# Revit family: Casement_41_E_Side_Hung_SD_Custom
name_source: partatom
category: Windows
revit_build: Autodesk Revit 2014 (Build: 20130308_1515(x64)
units: mm (PartAtom-declared; Revit-internal decimal feet)

## types (1)
- 41-TypeE-S-SD-Custom
    Corrected Mullion Configuration = 2 mm  [stored 0.00656168 ft]
    Description = Window 41mm, Type E, Side hung, Standard sash, Custom
    Frame Profile Thickness = 41 mm  [stored 0.134514 ft]
    Heavy Duty Sash = No
    Limit Fixed Pane Height Max = 3000 mm  [stored 9.84252 ft]
    Limit Fixed Pane Height Min = 200 mm  [stored 0.656168 ft]
    Limit Fixed Pane Width Max = 3000 mm  [stored 9.84252 ft]
    Limit Fixed Pane Width Min = 200 mm  [stored 0.656168 ft]
    Limit Sash Height Max = 1500 mm  [stored 4.92126 ft]
    Limit Sash Height Min = 300 mm  [stored 0.984252 ft]
    Limit Sash Width Max = 700 mm  [stored 2.29659 ft]
    Limit Sash Width Min = 300 mm  [stored 0.984252 ft]
    Manufacturer = Crealco
    Max System DG Unit Thickness = 25 mm  [stored 0.082021 ft]
    Model = Casement 41
    Rough Width = 3 mm  [stored 0.00984252 ft]
    Sash Side Gap = 44 mm
    Standard Mullion Different = No
    Standard Sash = Yes
    URL = http://www.crealco.co.za
    Wall Closure = By host

note: [stored X ft] marks values corroborated as IEEE doubles in the binary element streams (Revit-internal decimal feet)

## geometry (parser evidence)
native form markers: Sweep x14
no freeform markers — native parametric forms only
